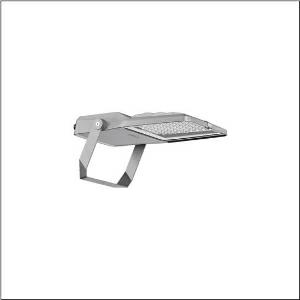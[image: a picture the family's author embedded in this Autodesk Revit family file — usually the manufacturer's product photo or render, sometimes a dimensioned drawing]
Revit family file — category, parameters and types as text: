
# Revit family: floodlight_fl_21_iq_mini___rs12_5xa7772c3b1a_483e
name_source: partatom
category: Lighting Fixtures
units: mm (PartAtom-declared; Revit-internal decimal feet)

## family parameters
Cut with Voids When Loaded = No
Host = Face
Light Source = No
Part Type = Normal
Room Calculation Point = No
Round Connector Dimension = Use Diameter
Shared = No

## types (1)
- --- (1 x LED, 10620 lm, 87.2 W, 3000K)
    Apparent Load = 87 VA
    CIE Flux Codes = 79 92 99 100 100
    Color Rendering = 80
    Color Temperature = 3000K
    Default Elevation = 1800 mm
    Description = Floodlight FL 21 iQ mini, floodlight, primary light control with lens, of PMMA, primary optical cover: protective disc, of toughened safety glass, transparent, light distribution: RS12, light emission: direct distribution, installation type: surface-mounted, lamps: LED, High Power LED, rated values: 10.620lm | 87,2W | 121,8lm/W (begin service life); end service life: 10.620lm | 92,1W; at 50% lumin. flux: 5.310lm | 40,1W | 132,4lm/W, colour temperature: 3000K, colour rendering: CRI > 80, light colour: 830, light setting 1 begin service life: 100% | 10.620lm | 87,2W | 121,8lm/W | 3.000K, light setting 1 end service life: 92,1W, further light settings possible, control: Street-Remote, Auto-Match, Temp-Guard, Night-Set, Smart-Wire, Desk-Remote (wireless, voltage-free reading and setting of iQ features in the workshop via application-optimized NFC function/RFID function), optimised constant luminous flux control (CLO 2.0), pre-setting: linear dimming characteristic, with terminal, 6-pole, mains connection: 220..240V, AC, 50/60Hz, luminaire housing, of diecast aluminium, powder-coated, SITECO metallic grey (DB 702S), corrosivity category C5 mid according to DIN EN ISO 12944suitable for swimming poolschlorine-resistant, sealing non-destructively replaceable, mounting bracket, of steel, galvanised, powder-coated, SITECO metallic grey (DB 702S), protection rating (complete): IP66, insulation class (complete): insulation class II (safety insulation), certification: CE, ENEC, VDE, protection symbol: D, impact resistance: IK08, permissible operating ambient temperature: -40..+40°C, permissible operating ambient temperature for outdoor applications: -40..+50°C, standard: DIN EN 12944, LABS conformity tested according to VDMA 24364:2018-05, packaging unit: 1 piece

Light Distribution: RS12
    Height = 70 mm
    Lamp = 1 x LED
    Lamp Light Flux = 10620 lm
    Lamp Power = 87.2 W
    Lamp count = 1
    Length = 485 mm
    Luminous efficacy = 122 lm/W
    Manufacturer = Siteco
    ModVariant = No
    Model = 5XA7772C3B1A
    Number of Poles = 1
    OnlyDefault = Yes
    Power Factor = 1
    Product Name = Floodlight FL 21 iQ mini | RS12
    Product group = floodlight | pylon annexe
    ProductGroupID = 6201
    Protection Class = Protection class II
    Protection Degree = IP 66
    RLX_Detail_Level = 1
    RLX_Emergency_Light_Flux = 0 lm
    RLX_Emergency_Type = 0
    RLX_Emergency_Type_DB = No
    RlxData = <blob elided: 91229 chars, md5=824bc624>
    Socket = socket
    Standby Power = 0 W
    System Light Flux = 10620 lm
    System Power = 87 W
    Type Comments = factory setting: luminous flux: 100 % | dim-lin: 254 | 456 mA
    Type Image = l_1006845.jpg
    URL = http://relux.com
    VarID = @adj_167077
    Voltage = 0 V
    Weight = 0.00 kg
    Width = 337 mm

## geometry (parser evidence)
native form markers: Blend x4, Sweep x15
no freeform markers — native parametric forms only
